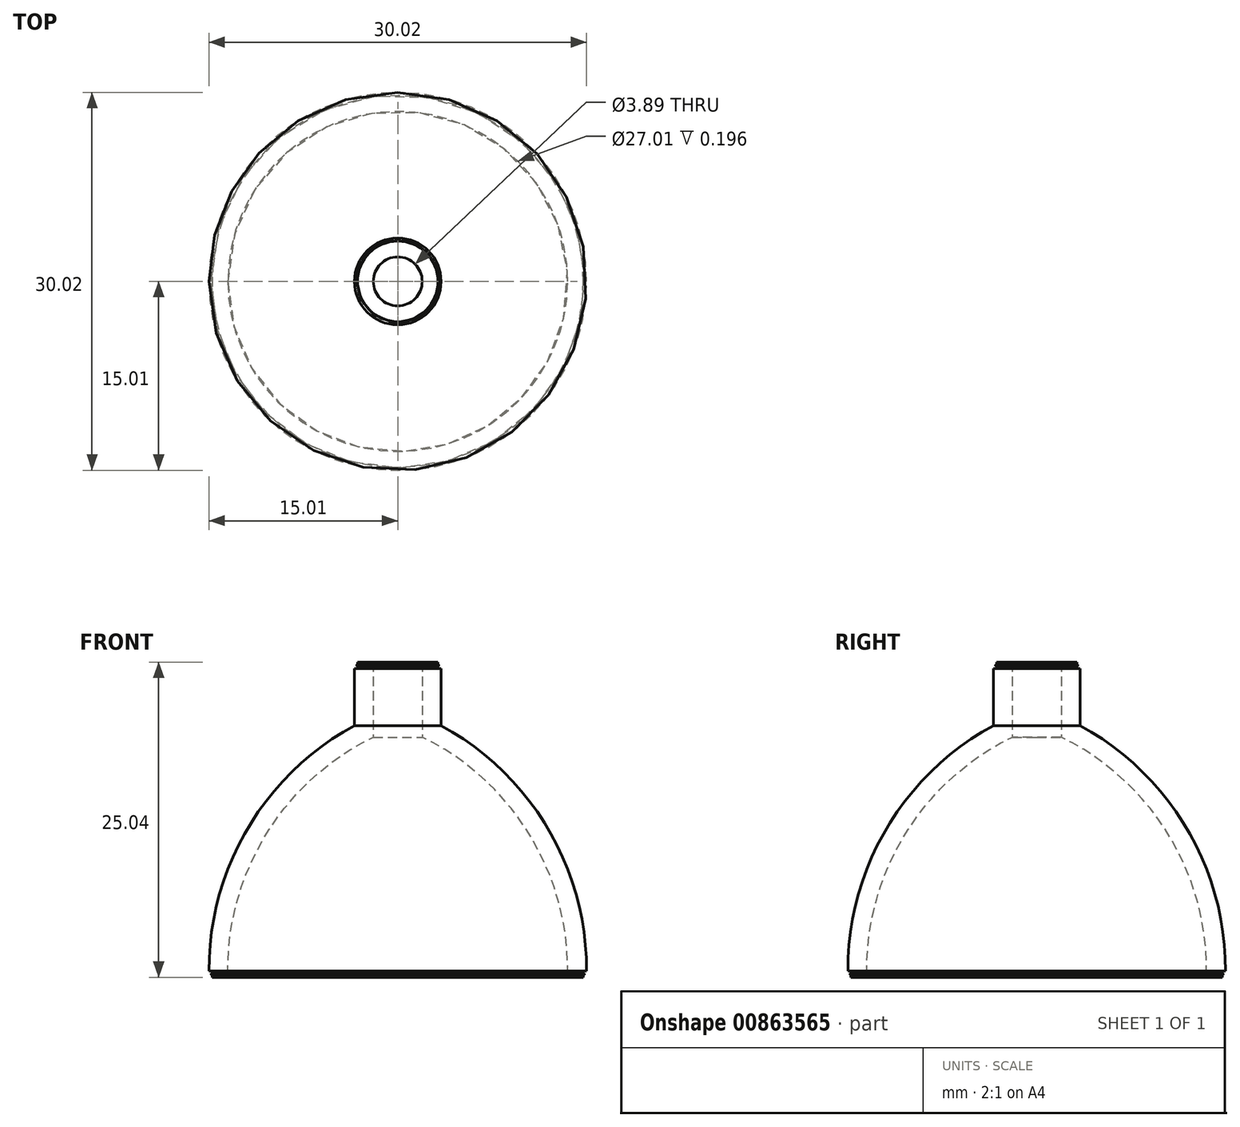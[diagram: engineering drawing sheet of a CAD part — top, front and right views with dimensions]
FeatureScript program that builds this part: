
annotation { "Feature Type Name" : "Feature", "Feature Type Description" : "" }
export const myFeature = defineFeature(function(context is Context, id is Id, definition is map)
    precondition{}
    {
        {
            var Q0;
            Q0=qCreatedBy(makeId("Front.planeOp"),FACE);
            var sketch = newSketch(context, id + "F0", { "sketchPlane" : qUnion([Q0])});
            skArc(sketch, "E0", {"start": v(-3.45, 20) * mm, "mid": v(-11.92, 11.85) * mm, "end": v(-15, 0.5) * mm});
            skLineSegment(sketch, "E1", {"start": v(-3.45, 20) * mm, "end": v(-3.45, 24.54) * mm});
            skArc(sketch, "E2.0", {"start": v(-1.95, 19.09) * mm, "mid": v(-10.48, 11.33) * mm, "end": v(-13.5, 0.2) * mm});
            skLineSegment(sketch, "E2.1", {"start": v(-1.95, 19.09) * mm, "end": v(-1.95, 24.59) * mm});
            skLineSegment(sketch, "E3", {"start": v(-14.76, 0) * mm, "end": v(-13.5, 0) * mm});
            skLineSegment(sketch, "E4", {"start": v(-13.5, 0) * mm, "end": v(-13.5, 0.2) * mm});
            skLineSegment(sketch, "E5", {"start": v(-3.2, 25.04) * mm, "end": v(-1.95, 25.04) * mm});
            skLineSegment(sketch, "E6", {"start": v(-1.95, 25.04) * mm, "end": v(-1.95, 24.59) * mm});
            skLineSegment(sketch, "E7", {"start": v(0, 0) * mm, "end": v(0, 25) * mm, "construction": true});
            skLineSegment(sketch, "E8", {"start": v(-2.4, 25.04) * mm, "end": v(-2.4, 18.86) * mm});
            skLineSegment(sketch, "E9", {"start": v(-3.45, 24.54) * mm, "end": v(-3.2, 24.54) * mm});
            skLineSegment(sketch, "E10", {"start": v(-3.2, 24.54) * mm, "end": v(-3.2, 25.04) * mm});
            skLineSegment(sketch, "E11", {"start": v(-14.76, 0) * mm, "end": v(-14.76, 0.5) * mm});
            skLineSegment(sketch, "E12", {"start": v(-14.76, 0.5) * mm, "end": v(-15, 0.5) * mm});
            skArc(sketch, "E13", {"start": v(-14.76, 0.33) * mm, "mid": v(-14.83, 0.25) * mm, "end": v(-14.76, 0.18) * mm});
            skPoint(sketch, "E14.orphan", {"position": v(-15, 0) * mm});
            skArc(sketch, "E15", {"start": v(-3.2, 24.86) * mm, "mid": v(-3.27, 24.79) * mm, "end": v(-3.2, 24.71) * mm});
            skSolve(sketch);
        }
        {
            var Q0;
            Q0 = qSketchRegion(id + "F0", true);
            var Q1;
            Q1=sQuery(id+"F0.wireOp",EDGE,"E7");
            revolve(context, id + "F1", {"surfaceOperationType" : NewSurfaceOperationType.NEW, "entities" : qUnion([Q0]), "axis" : qUnion([Q1]), "revolveType" : RevolveType.FULL});
        }
    });
